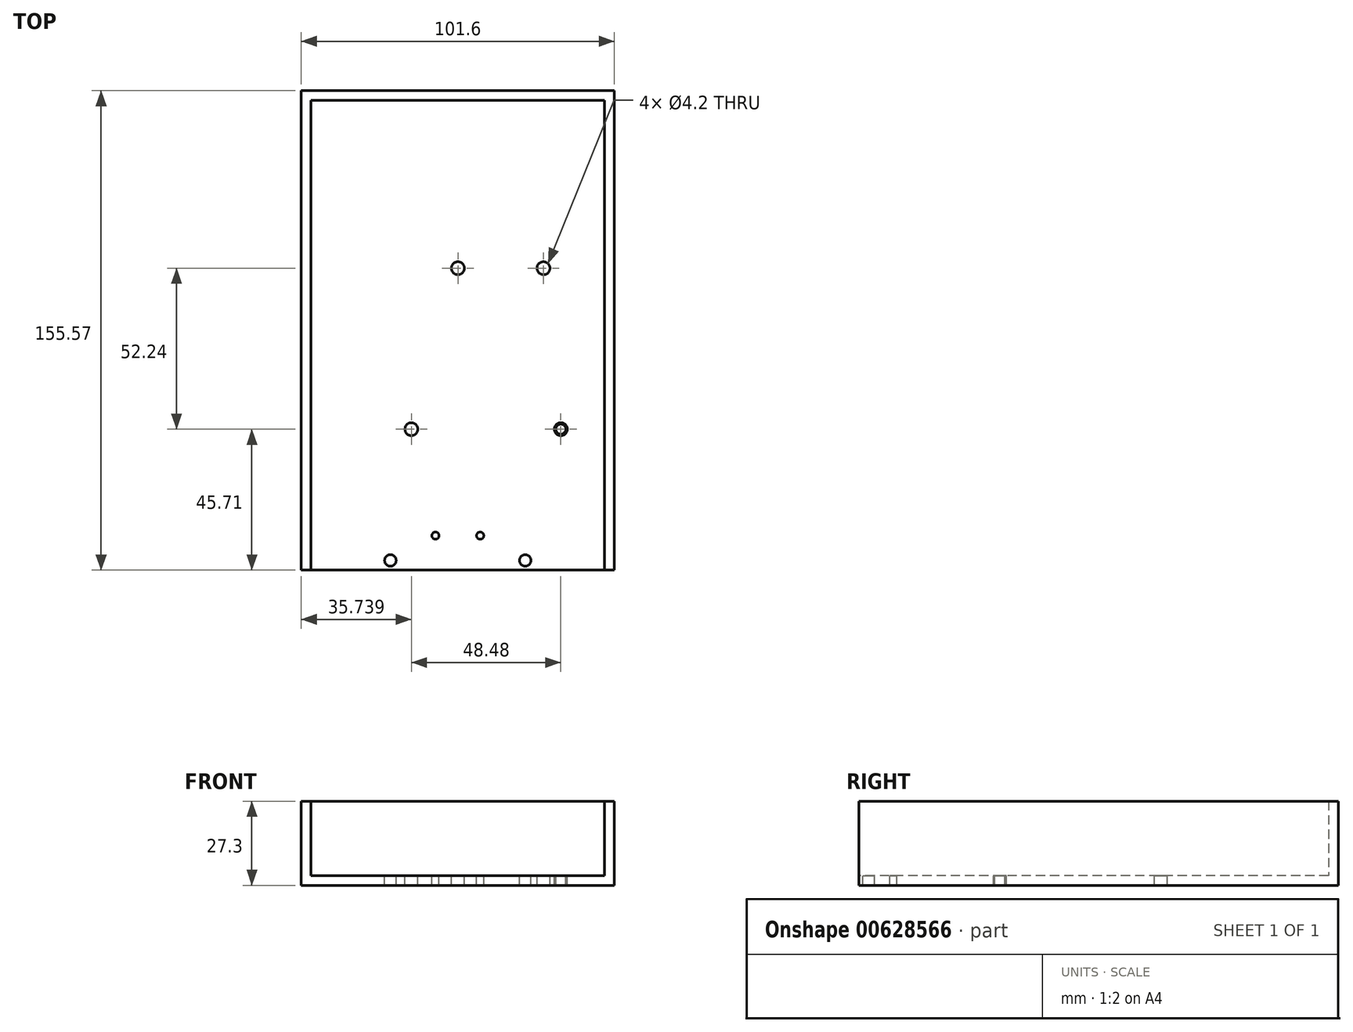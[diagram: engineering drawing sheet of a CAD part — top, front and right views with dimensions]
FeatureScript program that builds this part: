
annotation { "Feature Type Name" : "Feature", "Feature Type Description" : "" }
export const myFeature = defineFeature(function(context is Context, id is Id, definition is map)
    precondition{}
    {
        {
            var Q0;
            Q0=qCreatedBy(makeId("Top.planeOp"),FACE);
            var sketch = newSketch(context, id + "F0", { "sketchPlane" : qUnion([Q0])});
            skLineSegment(sketch, "E0.bottom", {"start": v(-50.8, 78.03) * mm, "end": v(50.8, 78.03) * mm});
            skLineSegment(sketch, "E0.top", {"start": v(-50.8, -74.37) * mm, "end": v(50.8, -74.37) * mm});
            skLineSegment(sketch, "E0.left", {"start": v(-50.8, 78.03) * mm, "end": v(-50.8, -74.37) * mm});
            skLineSegment(sketch, "E0.right", {"start": v(50.8, 78.03) * mm, "end": v(50.8, -74.37) * mm});
            skSolve(sketch);
        }
        {
            var Q0;
            Q0 = qSketchRegion(id + "F0", true);
            extrude(context, id + "F1", {"entities" : qUnion([Q0]), "depth" : 3.17 * mm, "offsetDistance" : 25.4 * mm});
        }
        {
            var Q0;
            Q0=makeQuery(id+"F1.opExtrude","CAP_FACE",FACE,{"disambiguationData":[OSD([sQuery(id+"F0.wireOp",EDGE,"E0.bottom"),sQuery(id+"F0.wireOp",EDGE,"E0.top"),sQuery(id+"F0.wireOp",EDGE,"E0.left"),sQuery(id+"F0.wireOp",EDGE,"E0.right")])],"isStart":false});
            var sketch = newSketch(context, id + "F2", { "sketchPlane" : qUnion([Q0])});
            skLineSegment(sketch, "E1.bottom", {"start": v(-50.8, 78.03) * mm, "end": v(-47.63, 78.03) * mm});
            skLineSegment(sketch, "E1.top", {"start": v(-50.8, -74.37) * mm, "end": v(-47.62, -74.37) * mm});
            skLineSegment(sketch, "E1.left", {"start": v(-50.8, 78.03) * mm, "end": v(-50.8, -74.37) * mm});
            skLineSegment(sketch, "E1.right", {"start": v(-47.63, 78.03) * mm, "end": v(-47.62, -74.37) * mm});
            skLineSegment(sketch, "E2.bottom", {"start": v(47.62, 78.03) * mm, "end": v(50.8, 78.03) * mm});
            skLineSegment(sketch, "E2.top", {"start": v(47.63, -74.37) * mm, "end": v(50.8, -74.37) * mm});
            skLineSegment(sketch, "E2.left", {"start": v(47.62, 78.03) * mm, "end": v(47.63, -74.37) * mm});
            skLineSegment(sketch, "E2.right", {"start": v(50.8, 78.03) * mm, "end": v(50.8, -74.37) * mm});
            skSolve(sketch);
        }
        {
            var Q0;
            Q0=makeQuery(id+"F2.imprint","IMPRINT",FACE,{"disambiguationData":[TD([[makeQuery(id+"F2.imprint","IMPRINT",EDGE,{"derivedFrom":sQuery(id+"F2.wireOp",EDGE,"E2.bottom")}),-1.0]])]});
            var Q1;
            Q1=makeQuery(id+"F2.imprint","IMPRINT",FACE,{"disambiguationData":[TD([[makeQuery(id+"F2.imprint","IMPRINT",EDGE,{"derivedFrom":sQuery(id+"F2.wireOp",EDGE,"E1.bottom")}),-1.0]])]});
            extrude(context, id + "F3", {"entities" : qUnion([Q0, Q1]), "operationType" : NewBodyOperationType.ADD, "depth" : 24.13 * mm, "offsetDistance" : 25.4 * mm});
        }
        {
            var Q0;
            Q0=makeQuery(id+"F3.boolean.opBoolean","MERGE",FACE,{"derivedFrom":[makeQuery(id+"F1.opExtrude","SWEPT_FACE",FACE,{"disambiguationData":[OSD([sQuery(id+"F0.wireOp",EDGE,"E0.bottom")])]}),makeQuery(id+"F3.opExtrude","SWEPT_FACE",FACE,{"disambiguationData":[OSD([sQuery(id+"F2.wireOp",EDGE,"E1.bottom")])]}),makeQuery(id+"F3.opExtrude","SWEPT_FACE",FACE,{"disambiguationData":[OSD([sQuery(id+"F2.wireOp",EDGE,"E2.bottom")])]})]});
            var sketch = newSketch(context, id + "F4", { "sketchPlane" : qUnion([Q0])});
            skLineSegment(sketch, "E3.bottom", {"start": v(-50.8, 27.3) * mm, "end": v(50.8, 27.3) * mm});
            skLineSegment(sketch, "E3.top", {"start": v(-50.8, 0) * mm, "end": v(50.8, 0) * mm});
            skLineSegment(sketch, "E3.left", {"start": v(-50.8, 27.3) * mm, "end": v(-50.8, 0) * mm});
            skLineSegment(sketch, "E3.right", {"start": v(50.8, 27.3) * mm, "end": v(50.8, 0) * mm});
            skSolve(sketch);
        }
        {
            var Q0;
            Q0 = qSketchRegion(id + "F4", true);
            extrude(context, id + "F5", {"entities" : qUnion([Q0]), "operationType" : NewBodyOperationType.ADD, "depth" : 3.17 * mm, "offsetDistance" : 25.4 * mm});
        }
        {
            var Q0;
            Q0=makeQuery(id+"F1.opExtrude","CAP_FACE",FACE,{"disambiguationData":[OSD([sQuery(id+"F0.wireOp",EDGE,"E0.bottom"),sQuery(id+"F0.wireOp",EDGE,"E0.top"),sQuery(id+"F0.wireOp",EDGE,"E0.left"),sQuery(id+"F0.wireOp",EDGE,"E0.right")])],"isStart":false});
            var sketch = newSketch(context, id + "F6", { "sketchPlane" : qUnion([Q0])});
            skCircle(sketch, "E4", {"center": v(-21.88, -71.25) * mm, "radius": 1.88 * mm});
            skCircle(sketch, "E5.MirrorC", {"center": v(21.88, -71.25) * mm, "radius": 1.88 * mm});
            skCircle(sketch, "E6", {"center": v(-7.25, -63.2) * mm, "radius": 1.18 * mm});
            skCircle(sketch, "E7.MirrorC", {"center": v(7.25, -63.2) * mm, "radius": 1.18 * mm});
            skCircle(sketch, "E8", {"center": v(-15.06, -28.66) * mm, "radius": 2.1 * mm});
            skCircle(sketch, "E9", {"center": v(27.79, 23.58) * mm, "radius": 2.1 * mm});
            skCircle(sketch, "E10", {"center": v(0.04, 23.58) * mm, "radius": 2.1 * mm});
            skCircle(sketch, "E11.MirrorC", {"center": v(33.42, -28.66) * mm, "radius": 2.1 * mm});
            skCircle(sketch, "E12", {"center": v(0.04, 23.58) * mm, "radius": 1.63 * mm});
            skCircle(sketch, "E13", {"center": v(27.79, 23.58) * mm, "radius": 1.63 * mm});
            skCircle(sketch, "E14", {"center": v(-15.06, -28.66) * mm, "radius": 1.63 * mm});
            skCircle(sketch, "E15.MirrorC", {"center": v(33.42, -28.66) * mm, "radius": 1.63 * mm});
            skSolve(sketch);
        }
        {
            var Q0;
            Q0 = qSketchRegion(id + "F6", true);
            var Q1;
            Q1=makeQuery(id+"F6.imprint","IMPRINT",FACE,{"disambiguationData":[TD([[makeQuery(id+"F6.imprint","IMPRINT",EDGE,{"derivedFrom":sQuery(id+"F6.wireOp",EDGE,"E13")}),1.0]])]});
            var Q2;
            Q2=makeQuery(id+"F6.imprint","IMPRINT",FACE,{"disambiguationData":[TD([[makeQuery(id+"F6.imprint","IMPRINT",EDGE,{"derivedFrom":sQuery(id+"F6.wireOp",EDGE,"E15.MirrorC")}),-1.0]])]});
            var Q3;
            Q3=makeQuery(id+"F6.imprint","IMPRINT",FACE,{"disambiguationData":[TD([[makeQuery(id+"F6.imprint","IMPRINT",EDGE,{"derivedFrom":sQuery(id+"F6.wireOp",EDGE,"E14")}),1.0]])]});
            var Q4;
            Q4=makeQuery(id+"F6.imprint","IMPRINT",FACE,{"disambiguationData":[TD([[makeQuery(id+"F6.imprint","IMPRINT",EDGE,{"derivedFrom":sQuery(id+"F6.wireOp",EDGE,"E12")}),1.0]])]});
            extrude(context, id + "F7", {"entities" : qUnion([Q0, Q1, Q2, Q3, Q4]), "operationType" : NewBodyOperationType.REMOVE, "endBound" : BoundingType.UP_TO_NEXT, "oppositeDirection" : true, "depth" : 25.4 * mm, "offsetDistance" : 25.4 * mm});
        }
    });
